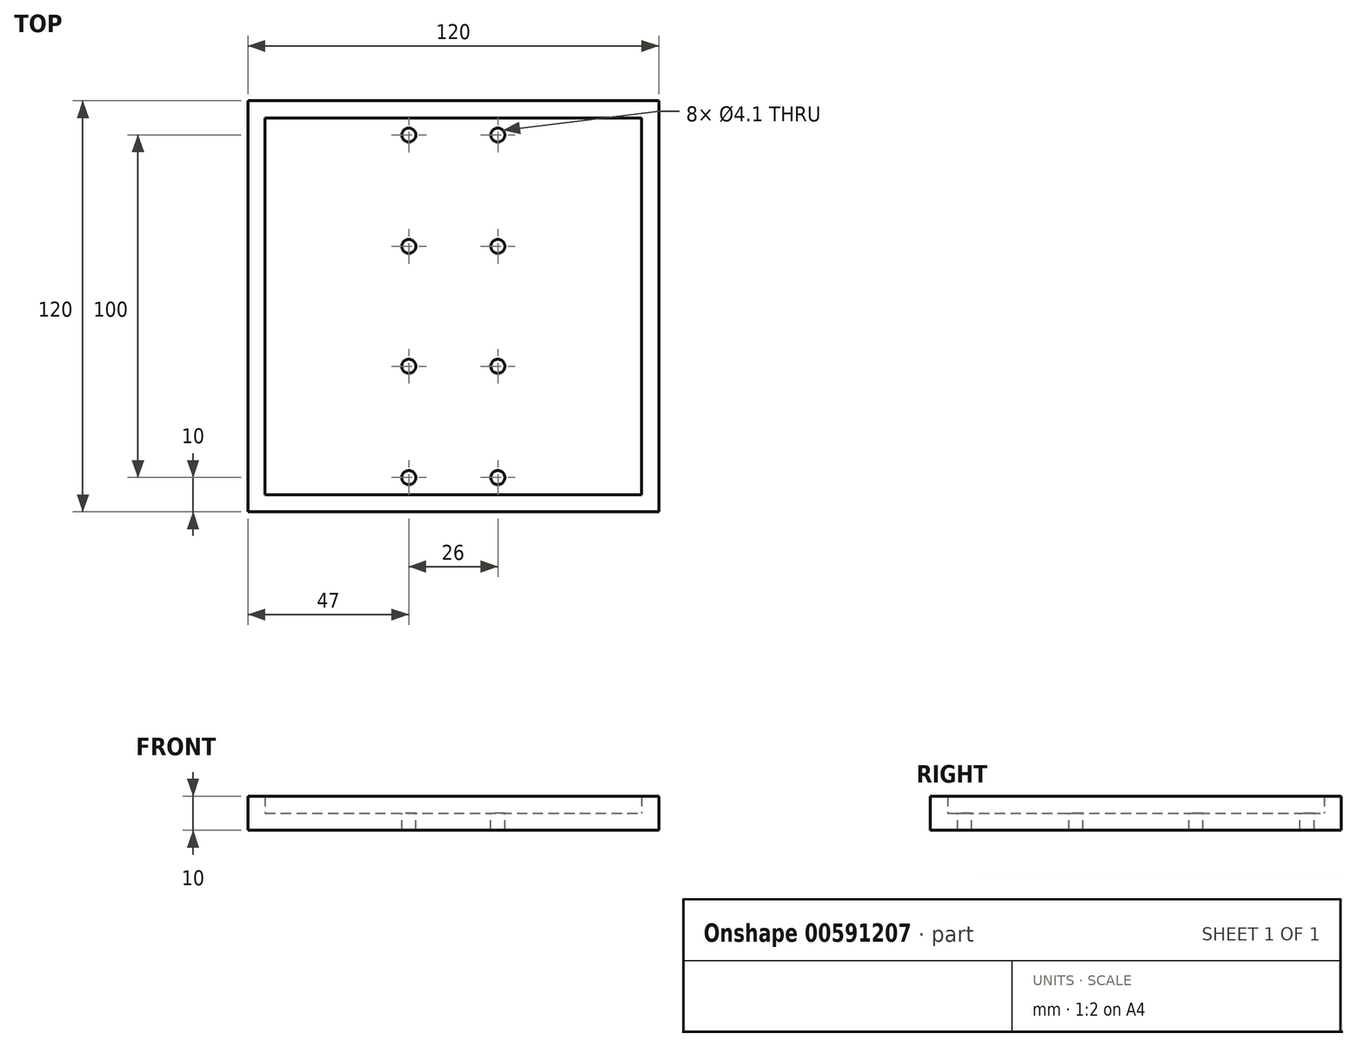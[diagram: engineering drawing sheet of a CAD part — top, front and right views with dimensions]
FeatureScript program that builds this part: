
annotation { "Feature Type Name" : "Feature", "Feature Type Description" : "" }
export const myFeature = defineFeature(function(context is Context, id is Id, definition is map)
    precondition{}
    {
        {
            var Q0;
            Q0=qCreatedBy(makeId("Top.planeOp"),FACE);
            var sketch = newSketch(context, id + "F0", { "sketchPlane" : qUnion([Q0])});
            skLineSegment(sketch, "E0.bottom", {"start": v(-60, 60) * mm, "end": v(60, 60) * mm});
            skLineSegment(sketch, "E0.top", {"start": v(-60, -60) * mm, "end": v(60, -60) * mm});
            skLineSegment(sketch, "E0.left", {"start": v(-60, 60) * mm, "end": v(-60, -60) * mm});
            skLineSegment(sketch, "E0.right", {"start": v(60, 60) * mm, "end": v(60, -60) * mm});
            skPoint(sketch, "E0.middle", {"position": v(0, 0) * mm});
            skCircle(sketch, "E1", {"center": v(-13, 50) * mm, "radius": 2.05 * mm});
            skCircle(sketch, "E2", {"center": v(13, 50) * mm, "radius": 2.05 * mm});
            skCircle(sketch, "E3", {"center": v(-13, 17.5) * mm, "radius": 2.05 * mm});
            skCircle(sketch, "E4", {"center": v(13, 17.5) * mm, "radius": 2.05 * mm});
            skCircle(sketch, "E5", {"center": v(-13, -50) * mm, "radius": 2.05 * mm});
            skCircle(sketch, "E6", {"center": v(13, -50) * mm, "radius": 2.05 * mm});
            skCircle(sketch, "E7", {"center": v(-13, -17.5) * mm, "radius": 2.05 * mm});
            skCircle(sketch, "E8", {"center": v(13, -17.5) * mm, "radius": 2.05 * mm});
            skSolve(sketch);
        }
        {
            var Q0;
            Q0 = qSketchRegion(id + "F0", true);
            extrude(context, id + "F1", {"entities" : qUnion([Q0]), "oppositeDirection" : true, "depth" : 5 * mm, "offsetDistance" : 25 * mm});
        }
        {
            var Q0;
            Q0=qCreatedBy(makeId("Top.planeOp"),FACE);
            var sketch = newSketch(context, id + "F2", { "sketchPlane" : qUnion([Q0])});
            skLineSegment(sketch, "E9.bottom", {"start": v(-60, 60) * mm, "end": v(60, 60) * mm});
            skLineSegment(sketch, "E9.top", {"start": v(-60, -60) * mm, "end": v(60, -60) * mm});
            skLineSegment(sketch, "E9.left", {"start": v(-60, 60) * mm, "end": v(-60, -60) * mm});
            skLineSegment(sketch, "E9.right", {"start": v(60, 60) * mm, "end": v(60, -60) * mm});
            skPoint(sketch, "E9.middle", {"position": v(0, 0) * mm});
            skLineSegment(sketch, "E10", {"start": v(55, 55) * mm, "end": v(55, -55) * mm});
            skLineSegment(sketch, "E11", {"start": v(55, -55) * mm, "end": v(-55, -55) * mm});
            skLineSegment(sketch, "E12", {"start": v(-55, -55) * mm, "end": v(-55, 55) * mm});
            skLineSegment(sketch, "E13", {"start": v(-55, 55) * mm, "end": v(55, 55) * mm});
            skSolve(sketch);
        }
        {
            var Q0;
            Q0 = qSketchRegion(id + "F2", true);
            extrude(context, id + "F3", {"entities" : qUnion([Q0]), "operationType" : NewBodyOperationType.ADD, "depth" : 5 * mm, "offsetDistance" : 25 * mm});
        }
    });
